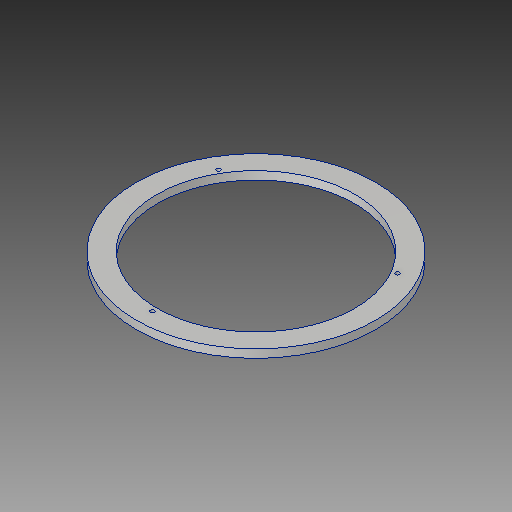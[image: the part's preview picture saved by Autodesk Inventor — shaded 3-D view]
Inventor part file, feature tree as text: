
AUTODESK INVENTOR PART (.ipt)
format: ipt  version: 2019 (Build 230136000, 136)  size: 124,416 bytes
history: native  units: mm
features: sketch x2, extrude x1, hole x1
ambient origin geometry x8: Origin, YZ Plane, XZ Plane, XY Plane, X Axis, Y Axis, Z Axis, Center Point
bodies: Solid1 (feature_tree)
feature tree (4):
  extrude  "Extrusion1"  Depth=248.0mm
  hole  "Hole1"  [1 undecoded]
  sketch  "Sketch2"  dims[d0=300.0mm d1=248.0mm]
  sketch  "Sketch3"  dims[d2=10.2mm d3=0.0mm d4=5.0mm d5=6.0mm d6=4.0mm d7=2.0mm d8=90.0deg d9=8.0mm d10=20.594885mm d11=30.0mm d13=360.0deg d15=130.0mm]
note: 1 required parameter value undecoded (feature->parameter linkage not recoverable at this tier; creation-order binding heuristic only, values carry confidence <= 0.55)
